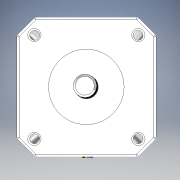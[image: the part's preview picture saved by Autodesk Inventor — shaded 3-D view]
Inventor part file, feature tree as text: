
AUTODESK INVENTOR PART (.ipt)
format: ipt  version: 2016 (Build 200138000, 138)  size: 1,078,272 bytes
history: native  units: mm
features: extrude x12, sketch x4, hole x4, fillet x4, chamfer x2, plane x1, pattern_linear x1, projected_geometry x1
ambient origin geometry x8: Origin, YZ Plane, XZ Plane, XY Plane, X Axis, Y Axis, Z Axis, Center Point
bodies: Solid1 (feature_tree)
feature tree (29):
  sketch  "Sketch1"  dims[d0=7.0mm d1=22.0mm]
  extrude  "Extrusion1"  Depth=22.0mm
  extrude  "Extrusion2"  Depth=31.0mm
  extrude  "Extrusion3"  Depth=3.0mm
  plane  "Work Plane2"
  extrude  "Extrusion7"  Depth=10.0mm
  extrude  "Extrusion8"  Depth=10.0mm
  chamfer  "Chamfer1"  Distance=42.0mm
  pattern_linear  "Rectangular Pattern2"  Spacing1=42.0mm  [1 undecoded]
  hole  "Hole1"  [1 undecoded]
  hole  "Hole2"  [1 undecoded]
  hole  "Hole3"  [1 undecoded]
  hole  "Hole4"  [1 undecoded]
  extrude  "Extrusion9"  Depth=10.0mm
  fillet  "Fillet1"  Radius=24.0mm
  fillet  "Fillet2"  Radius=2.0mm
  chamfer  "Chamfer2"  Distance=48.0mm
  fillet  "Fillet3"  [1 undecoded]
  sketch  "Sketch6"  dims[d10=3.0mm d11=3.0mm d12=3.0mm d39=42.0mm d40=42.0mm d41=135.0deg d42=51.618795mm d43=51.618795mm d44=25.809398mm d45=25.809398mm d46=24.0mm d47=0.0mm d48=2.0mm d49=0.0mm d50=48.0mm d51=0.0mm d60=-10.0mm d126=28.0mm d127=0.0mm d128=1.0mm d129=1.0mm d130=1.0mm d131=1.0mm d132=0.5mm d134=0.5mm d135=0.5mm d136=0.5mm d137=0.5mm d138=1.0mm d139=1.0mm d140=0.5mm d141=0.0mm d145=0.125mm d146=2.0mm d147=45.0deg d148=560.0mm d150=0.5mm d151=10.0mm d152=10.0mm d153=6.0mm d154=6.0mm d155=4.0mm d156=2.0mm d157=90.0deg d158=3.0mm d159=0.0mm d160=10.0mm d161=10.0mm d162=6.0mm d163=6.0mm d164=4.0mm d165=2.0mm d166=90.0deg d167=3.0mm d168=0.0mm d169=10.0mm d170=10.0mm d171=6.0mm d172=6.0mm d173=4.0mm d174=2.0mm d175=90.0deg d176=3.0mm d177=0.0mm d178=10.0mm d179=10.0mm d180=6.0mm d181=6.0mm d182=4.0mm d183=2.0mm d184=90.0deg d185=3.0mm d186=0.0mm d187=48.0mm d188=0.0mm d189=47.0mm d190=0.0mm d191=1.0mm d192=1.0mm d193=0.5mm d194=2.0mm d195=45.0deg d196=0.5mm d197=1.2mm d198=40.0mm d200=1.2mm d201=10.0mm d203=10.0mm d205=2.5mm d206=2.5mm d207=1.0mm d208=0.0mm d209=0.3mm d210=10.0mm d211=0.0mm d212=10.0mm d213=0.0mm d214=10.0mm d215=0.0mm d216=10.0mm d217=0.0mm d218=0.2mm d219=5.0mm d220=0.0mm d221=0.0mm]
  extrude  "Extrusion10"  Depth=10.0mm TaperAngle=0.0deg
  fillet  "Fillet4"  Radius=1.0mm
  extrude  "Extrusion11"  Depth=10.0mm
  extrude  "Extrusion12"  Depth=10.0mm
  extrude  "Extrusion13"  Depth=10.0mm
  extrude  "Extrusion14"  Depth=10.0mm
  extrude  "Extrusion15"  Depth=10.0mm
  sketch  "Sketch4"  dims[d4=5.0mm d5=31.0mm]
  projected_geometry  "Projected Loop2"
  sketch  "Sketch5"  dims[d6=31.0mm d9=3.0mm]
note: 6 required parameter values undecoded (feature->parameter linkage not recoverable at this tier; creation-order binding heuristic only, values carry confidence <= 0.55)
